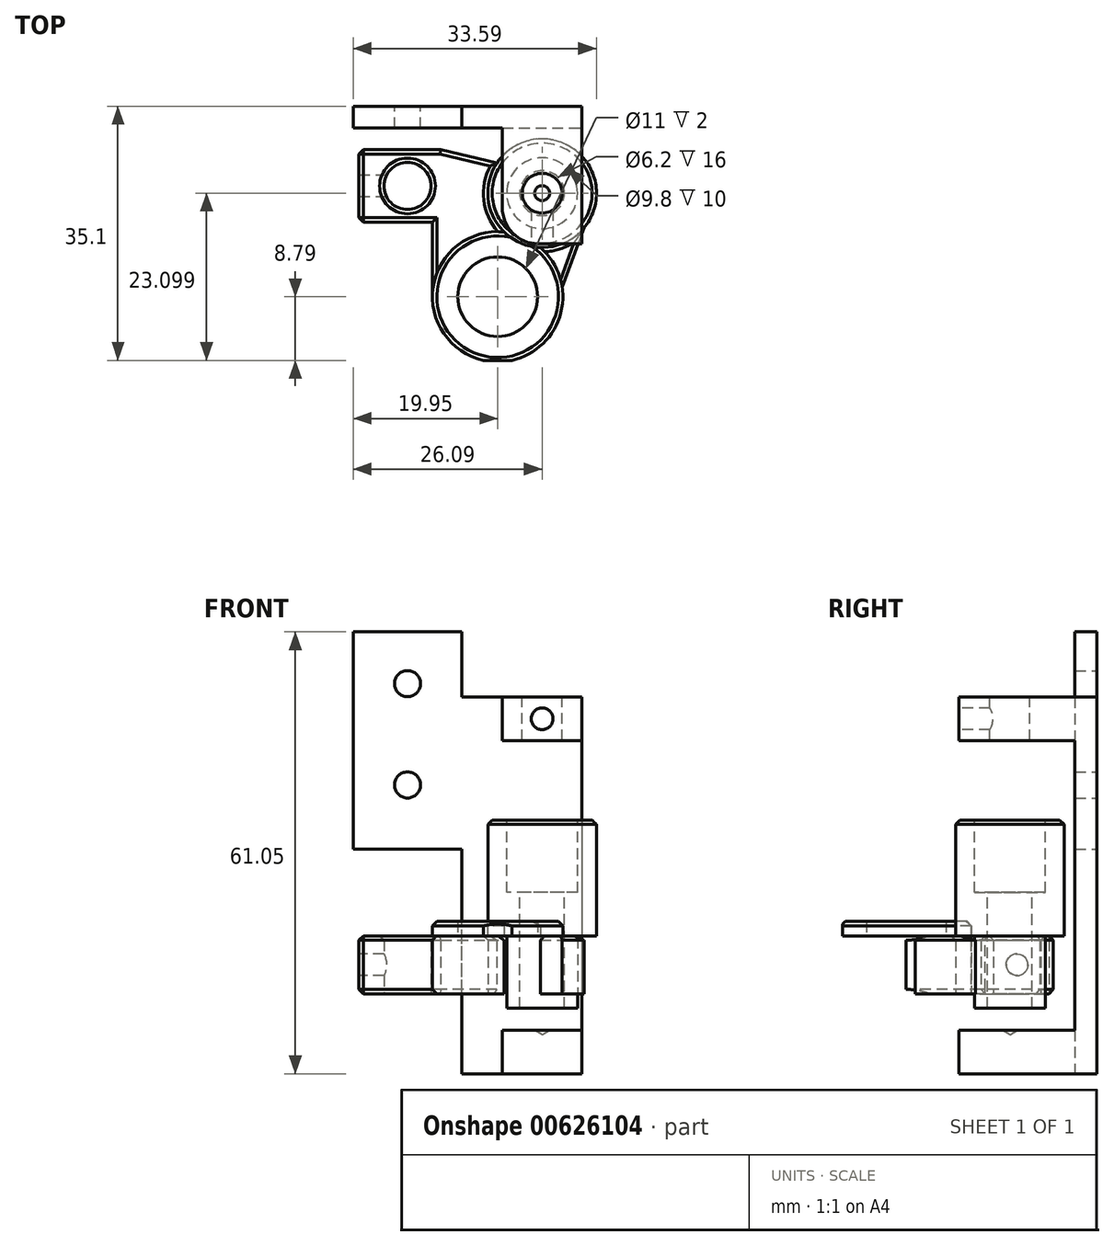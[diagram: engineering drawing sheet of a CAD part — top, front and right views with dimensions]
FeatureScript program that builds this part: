
annotation { "Feature Type Name" : "Feature", "Feature Type Description" : "" }
export const myFeature = defineFeature(function(context is Context, id is Id, definition is map)
    precondition{}
    {
        {
            var Q0;
            Q0=qCreatedBy(makeId("Top.planeOp"),FACE);
            var sketch = newSketch(context, id + "F0", { "sketchPlane" : qUnion([Q0])});
            skCircle(sketch, "E0", {"center": v(-12.45, 15.3) * mm, "radius": 3.25 * mm});
            skCircle(sketch, "E1", {"center": v(0, 0) * mm, "radius": 5.5 * mm});
            skCircle(sketch, "E2", {"center": v(6.14, 14.3) * mm, "radius": 4.9 * mm});
            skLineSegment(sketch, "E3", {"start": v(-26.15, 14.3) * mm, "end": v(35.58, 14.3) * mm, "construction": true});
            skLineSegment(sketch, "E4", {"start": v(-6.47, 0) * mm, "end": v(11.2, 0) * mm, "construction": true});
            skCircle(sketch, "E5", {"center": v(6.14, 14.3) * mm, "radius": 7.5 * mm});
            skLineSegment(sketch, "E6", {"start": v(0, 2.55) * mm, "end": v(0, -2.85) * mm, "construction": true});
            skLineSegment(sketch, "E7.bottom", {"start": v(-19.95, 22.8) * mm, "end": v(-4.95, 22.8) * mm, "construction": true});
            skLineSegment(sketch, "E7.top", {"start": v(-19.95, 7.8) * mm, "end": v(-4.95, 7.8) * mm, "construction": true});
            skLineSegment(sketch, "E7.right", {"start": v(-4.95, 22.8) * mm, "end": v(-4.95, 7.8) * mm, "construction": true});
            skLineSegment(sketch, "E8", {"start": v(-20.5, 15.3) * mm, "end": v(-2.43, 15.3) * mm, "construction": true});
            skLineSegment(sketch, "E9", {"start": v(-12.45, 21.65) * mm, "end": v(-12.45, 0) * mm, "construction": true});
            skLineSegment(sketch, "E10", {"start": v(-7.86, 20.3) * mm, "end": v(-19.16, 20.3) * mm});
            skLineSegment(sketch, "E11", {"start": v(-19.16, 20.3) * mm, "end": v(-19.16, 10.3) * mm});
            skLineSegment(sketch, "E12", {"start": v(-19.16, 10.3) * mm, "end": v(-9, 10.3) * mm});
            skCircle(sketch, "E13", {"center": v(6.14, 14.3) * mm, "radius": 3.1 * mm});
            skLineSegment(sketch, "E14", {"start": v(-19.95, 22.8) * mm, "end": v(-19.95, 7.8) * mm, "construction": true});
            skLineSegment(sketch, "E15", {"start": v(-9, 10.3) * mm, "end": v(-9, 0) * mm});
            skLineSegment(sketch, "E16", {"start": v(-7.86, 20.3) * mm, "end": v(-0.1, 18.47) * mm});
            skCircle(sketch, "E17", {"center": v(0, 0) * mm, "radius": 9 * mm});
            skLineSegment(sketch, "E18", {"start": v(8.9, 1.28) * mm, "end": v(11.93, 9.55) * mm});
            skLineSegment(sketch, "E19", {"start": v(-1.94, -8.79) * mm, "end": v(1.94, -8.79) * mm});
            skSolve(sketch);
        }
        {
            var Q0;
            Q0=makeQuery(id+"F0.imprint","IMPRINT",FACE,{"disambiguationData":[TD([[makeQuery(id+"F0.imprint","IMPRINT",EDGE,{"derivedFrom":sQuery(id+"F0.wireOp",EDGE,"E1")}),-1.0]])]});
            var Q1;
            {var subQ0=sQuery(id+"F0.wireOp",EDGE,"E17");var subQ1=sQuery(id+"F0.wireOp",EDGE,"E5");var subQ2=makeQuery(id+"F0.imprint","INTERSECT",VERTEX,{"disambiguationData":[OD(0.0)],"derivedFrom":[subQ1,subQ0]});Q1=makeQuery(id+"F0.imprint","IMPRINT",FACE,{"disambiguationData":[TD([[makeQuery(id+"F0.imprint","IMPRINT",EDGE,{"disambiguationData":[TD([[subQ2,-1.0]])],"derivedFrom":subQ1}),1.0]])]});}
            extrude(context, id + "F1", {"entities" : qUnion([Q0, Q1]), "endBound" : BoundingType.SYMMETRIC, "depth" : 12 * mm, "offsetDistance" : 25 * mm});
        }
        {
            var Q0;
            {var subQ0=sQuery(id+"F0.wireOp",EDGE,"E17");var subQ1=sQuery(id+"F0.wireOp",EDGE,"E5");var subQ2=makeQuery(id+"F0.imprint","INTERSECT",VERTEX,{"disambiguationData":[OD(0.0)],"derivedFrom":[subQ1,subQ0]});Q0=makeQuery(id+"F0.imprint","IMPRINT",FACE,{"disambiguationData":[TD([[makeQuery(id+"F0.imprint","IMPRINT",EDGE,{"disambiguationData":[TD([[subQ2,-1.0]])],"derivedFrom":subQ1}),1.0]])]});}
            var Q1;
            Q1=makeQuery(id+"F0.imprint","IMPRINT",FACE,{"disambiguationData":[TD([[makeQuery(id+"F0.imprint","IMPRINT",EDGE,{"derivedFrom":sQuery(id+"F0.wireOp",EDGE,"E2")}),-1.0]])]});
            var Q2;
            Q2=makeQuery(id+"F0.imprint","IMPRINT",FACE,{"disambiguationData":[TD([[makeQuery(id+"F0.imprint","IMPRINT",EDGE,{"derivedFrom":sQuery(id+"F0.wireOp",EDGE,"E2")}),1.0]])]});
            var Q3;
            Q3=makeQuery(id+"F1.opExtrude","CAP_FACE",FACE,{"disambiguationData":[OSD([sQuery(id+"F0.wireOp",EDGE,"E1"),sQuery(id+"F0.wireOp",EDGE,"E17")])],"isStart":true});
            extrude(context, id + "F2", {"entities" : qUnion([Q0, Q1, Q2]), "operationType" : NewBodyOperationType.ADD, "endBound" : BoundingType.UP_TO_SURFACE, "oppositeDirection" : true, "depth" : 20 * mm, "endBoundEntityFace" : qUnion([Q3]), "offsetDistance" : 25 * mm});
        }
        {
            var Q0;
            Q0=makeQuery(id+"F0.imprint","IMPRINT",FACE,{"disambiguationData":[TD([[makeQuery(id+"F0.imprint","IMPRINT",EDGE,{"derivedFrom":sQuery(id+"F0.wireOp",EDGE,"E0")}),-1.0]])]});
            var Q1;
            {var subQ0=sQuery(id+"F0.wireOp",EDGE,"E18");Q1=makeQuery(id+"F0.imprint","IMPRINT",FACE,{"disambiguationData":[TD([[makeQuery(id+"F0.imprint","IMPRINT",EDGE,{"derivedFrom":subQ0}),1.0]])]});}
            var Q2;
            Q2=makeQuery(id+"F1.opExtrude","CAP_FACE",FACE,{"disambiguationData":[OSD([sQuery(id+"F0.wireOp",EDGE,"E1"),sQuery(id+"F0.wireOp",EDGE,"E5"),sQuery(id+"F0.wireOp",EDGE,"E17")])],"isStart":false});
            extrude(context, id + "F3", {"entities" : qUnion([Q0, Q1]), "operationType" : NewBodyOperationType.ADD, "endBound" : BoundingType.SYMMETRIC, "depth" : 8 * mm, "endBoundEntityFace" : qUnion([Q2]), "offsetDistance" : 25 * mm});
        }
        {
            var Q0;
            {var subQ0=sQuery(id+"F0.wireOp",EDGE,"kT476SbK-n5dK-4PEZ-Ph8G-A7WMILJMmlgB");var subQ1=sQuery(id+"F0.wireOp",EDGE,"E5");var subQ2=makeQuery(id+"F0.imprint","INTERSECT",VERTEX,{"derivedFrom":[subQ1,subQ0]});Q0=makeQuery(id+"F0.imprint","IMPRINT",FACE,{"disambiguationData":[TD([[makeQuery(id+"F0.imprint","IMPRINT",EDGE,{"disambiguationData":[TD([[subQ2,-1.0]])],"derivedFrom":subQ1}),1.0]])]});}
            var Q1;
            Q1=makeQuery(id+"F0.imprint","IMPRINT",FACE,{"disambiguationData":[TD([[makeQuery(id+"F0.imprint","IMPRINT",EDGE,{"derivedFrom":sQuery(id+"F0.wireOp",EDGE,"E2")}),-1.0]])]});
            var Q2;
            Q2=makeQuery(id+"F0.imprint","IMPRINT",FACE,{"disambiguationData":[TD([[makeQuery(id+"F0.imprint","IMPRINT",EDGE,{"derivedFrom":sQuery(id+"F0.wireOp",EDGE,"E2")}),1.0]])]});
            var Q3;
            {var subQ0=sQuery(id+"F0.wireOp",EDGE,"E17");var subQ1=sQuery(id+"F0.wireOp",EDGE,"E5");var subQ2=makeQuery(id+"F0.imprint","INTERSECT",VERTEX,{"disambiguationData":[OD(0.0)],"derivedFrom":[subQ1,subQ0]});Q3=makeQuery(id+"F0.imprint","IMPRINT",FACE,{"disambiguationData":[TD([[makeQuery(id+"F0.imprint","IMPRINT",EDGE,{"disambiguationData":[TD([[subQ2,-1.0]])],"derivedFrom":subQ1}),1.0]])]});}
            var Q4;
            Q4=makeQuery(id+"F1.opExtrude","CAP_FACE",FACE,{"disambiguationData":[OSD([sQuery(id+"F0.wireOp",EDGE,"E1"),sQuery(id+"F0.wireOp",EDGE,"E17")])],"isStart":false});
            extrude(context, id + "F4", {"entities" : qUnion([Q0, Q1, Q2, Q3]), "operationType" : NewBodyOperationType.ADD, "depth" : 20 * mm, "endBoundEntityFace" : qUnion([Q4]), "offsetDistance" : 25 * mm});
        }
        {
            var Q0;
            Q0=makeQuery(id+"F4.opExtrude","CAP_FACE",FACE,{"disambiguationData":[OSD([sQuery(id+"F0.wireOp",EDGE,"E5"),sQuery(id+"F0.wireOp",EDGE,"E13")])],"isStart":false});
            var sketch = newSketch(context, id + "F5", { "sketchPlane" : qUnion([Q0])});
            skPoint(sketch, "E20.0", {"position": v(6.14, 14.3) * mm});
            skCircle(sketch, "E21.0", {"center": v(6.14, 14.3) * mm, "radius": 4.9 * mm});
            skCircle(sketch, "E22.0.0", {"center": v(6.14, 14.3) * mm, "radius": 7.5 * mm});
            skSolve(sketch);
        }
        {
            var Q0;
            Q0=makeQuery(id+"F5.imprint","IMPRINT",FACE,{"disambiguationData":[TD([[makeQuery(id+"F5.imprint","IMPRINT",EDGE,{"derivedFrom":sQuery(id+"F5.wireOp",EDGE,"E21.0")}),1.0]])]});
            extrude(context, id + "F6", {"entities" : qUnion([Q0]), "operationType" : NewBodyOperationType.REMOVE, "oppositeDirection" : true, "depth" : 10 * mm, "offsetDistance" : 25 * mm});
        }
        {
            var Q0;
            Q0=makeQuery(id+"F2.boolean.opBoolean","MERGE",FACE,{"derivedFrom":[makeQuery(id+"F1.opExtrude","CAP_FACE",FACE,{"disambiguationData":[OSD([sQuery(id+"F0.wireOp",EDGE,"E1"),sQuery(id+"F0.wireOp",EDGE,"E17"),sQuery(id+"F0.wireOp",EDGE,"E19")])],"isStart":true}),makeQuery(id+"F2.opExtrude","CAP_FACE",FACE,{"disambiguationData":[OSD([sQuery(id+"F0.wireOp",EDGE,"E5"),sQuery(id+"F0.wireOp",EDGE,"E13")])],"isStart":false})]});
            var sketch = newSketch(context, id + "F7", { "sketchPlane" : qUnion([Q0])});
            skCircle(sketch, "E23.0", {"center": v(6.14, -14.3) * mm, "radius": 4.9 * mm});
            skCircle(sketch, "E23.1", {"center": v(6.14, -14.3) * mm, "radius": 3.1 * mm});
            skCircle(sketch, "E24.0", {"center": v(6.14, -14.3) * mm, "radius": 3.9 * mm});
            skSolve(sketch);
        }
        {
            var Q0;
            Q0=makeQuery(id+"F7.imprint","IMPRINT",FACE,{"disambiguationData":[TD([[makeQuery(id+"F7.imprint","IMPRINT",EDGE,{"derivedFrom":sQuery(id+"F7.wireOp",EDGE,"E23.0")}),-1.0]])]});
            extrude(context, id + "F8", {"entities" : qUnion([Q0]), "operationType" : NewBodyOperationType.REMOVE, "oppositeDirection" : true, "depth" : 10 * mm, "offsetDistance" : 25 * mm});
        }
        {
            var Q0;
            Q0=makeQuery(id+"F3.opExtrude","SWEPT_FACE",FACE,{"disambiguationData":[OSD([sQuery(id+"F0.wireOp",EDGE,"E11")])]});
            var sketch = newSketch(context, id + "F9", { "sketchPlane" : qUnion([Q0])});
            skPoint(sketch, "E25.0", {"position": v(-15.3, 0) * mm});
            skSolve(sketch);
        }
        {
            var Q0;
            Q0=sQuery(id+"F9.wireOp",VERTEX,"E25.0");
            var Q1;
            Q1=makeQuery(id+"F1.opExtrude","SWEPT_BODY",BODY,{"disambiguationData":[OSD([sQuery(id+"F0.wireOp",EDGE,"E1"),sQuery(id+"F0.wireOp",EDGE,"E5"),sQuery(id+"F0.wireOp",EDGE,"kT476SbK-n5dK-4PEZ-Ph8G-A7WMILJMmlgB"),sQuery(id+"F0.wireOp",EDGE,"aIw4lDgL-LfnZ-en49-FZka-zHxeNgxKbi4w"),sQuery(id+"F0.wireOp",EDGE,"VI2pno59-77TE-V6qu-3BII-ZEAurTLzmaWP"),sQuery(id+"F0.wireOp",EDGE,"Tc2wsCnA-F8RX-Uh19-z4kL-r0QHivfHJg5U")])]});
            hole(context, id + "F10", {"style" : HoleStyle.SIMPLE, "endStyle" : HoleEndStyle.BLIND, "holeDiameter" : 3 * mm, "majorDiameter" : 5 * mm, "holeDepth" : 8 * mm, "isTappedThrough" : true, "tappedDepth" : 7 * mm, "tapClearance" : 6, "startFromSketch" : true, "locations" : qUnion([Q0]), "scope" : qUnion([Q1])});
        }
        {
            var Q0;
            Q0=makeQuery(id+"F1.opExtrude","SWEPT_FACE",FACE,{"disambiguationData":[OSD([sQuery(id+"F0.wireOp",EDGE,"E19")])]});
            var sketch = newSketch(context, id + "F11", { "sketchPlane" : qUnion([Q0])});
            skPoint(sketch, "E26.0", {"position": v(0, 0) * mm});
            skSolve(sketch);
        }
        {
            var Q0;
            Q0=sQuery(id+"F11.wireOp",VERTEX,"E26.0");
            var Q1;
            Q1=makeQuery(id+"F1.opExtrude","SWEPT_BODY",BODY,{"disambiguationData":[OSD([sQuery(id+"F0.wireOp",EDGE,"E1"),sQuery(id+"F0.wireOp",EDGE,"E5"),sQuery(id+"F0.wireOp",EDGE,"kT476SbK-n5dK-4PEZ-Ph8G-A7WMILJMmlgB"),sQuery(id+"F0.wireOp",EDGE,"aIw4lDgL-LfnZ-en49-FZka-zHxeNgxKbi4w"),sQuery(id+"F0.wireOp",EDGE,"VI2pno59-77TE-V6qu-3BII-ZEAurTLzmaWP"),sQuery(id+"F0.wireOp",EDGE,"Tc2wsCnA-F8RX-Uh19-z4kL-r0QHivfHJg5U")])]});
            hole(context, id + "F12", {"style" : HoleStyle.SIMPLE, "endStyle" : HoleEndStyle.BLIND, "holeDiameter" : 4.1 * mm, "majorDiameter" : 5 * mm, "holeDepth" : 8 * mm, "isTappedThrough" : true, "tappedDepth" : 7 * mm, "tapClearance" : 6, "startFromSketch" : true, "locations" : qUnion([Q0]), "scope" : qUnion([Q1])});
        }
        {
            var Q0;
            Q0=makeQuery(id+"F3.opExtrude","SWEPT_FACE",FACE,{"disambiguationData":[OSD([sQuery(id+"F0.wireOp",EDGE,"E10")])]});
            cPlane(context, id + "F13", {"entities" : qUnion([Q0]), "cplaneType" : CPlaneType.OFFSET, "offset" : 6 * mm, "width" : 150 * mm, "height" : 150 * mm});
        }
        {
            var Q0;
            Q0=qCreatedBy(id+"F13.planeOp",FACE);
            var sketch = newSketch(context, id + "F14", { "sketchPlane" : qUnion([Q0])});
            skLineSegment(sketch, "E27", {"start": v(19.95, 16) * mm, "end": v(19.95, 46) * mm});
            skLineSegment(sketch, "E28", {"start": v(-11.64, 36.98) * mm, "end": v(-11.64, -15.05) * mm});
            skLineSegment(sketch, "E29", {"start": v(-11.64, -15.05) * mm, "end": v(4.95, -15.05) * mm});
            skLineSegment(sketch, "E30", {"start": v(4.95, -15.05) * mm, "end": v(4.95, 16) * mm});
            skLineSegment(sketch, "E31", {"start": v(4.95, 16) * mm, "end": v(19.95, 16) * mm});
            skPoint(sketch, "E32.0", {"position": v(-6.14, 0) * mm});
            skLineSegment(sketch, "E33", {"start": v(-6.14, 34.02) * mm, "end": v(-6.14, -35.1) * mm, "construction": true});
            skLineSegment(sketch, "E34.bottom", {"start": v(-0.64, -9.05) * mm, "end": v(-11.64, -9.05) * mm});
            skLineSegment(sketch, "E34.top", {"start": v(-0.64, -15.05) * mm, "end": v(-11.64, -15.05) * mm});
            skLineSegment(sketch, "E34.left", {"start": v(-0.64, -9.05) * mm, "end": v(-0.64, -15.05) * mm});
            skLineSegment(sketch, "E34.right", {"start": v(-11.64, -9.05) * mm, "end": v(-11.64, -15.05) * mm});
            skLineSegment(sketch, "E35.bottom", {"start": v(-0.64, 36.98) * mm, "end": v(-11.64, 36.98) * mm});
            skLineSegment(sketch, "E35.top", {"start": v(-0.64, 30.98) * mm, "end": v(-11.64, 30.98) * mm});
            skLineSegment(sketch, "E35.left", {"start": v(-0.64, 36.98) * mm, "end": v(-0.64, 30.98) * mm});
            skLineSegment(sketch, "E35.right", {"start": v(-11.64, 36.98) * mm, "end": v(-11.64, 30.98) * mm});
            skPoint(sketch, "E36.0", {"position": v(12.45, 0) * mm});
            skLineSegment(sketch, "E37", {"start": v(12.45, 51.45) * mm, "end": v(12.45, -16.66) * mm, "construction": true});
            skLineSegment(sketch, "E38.0", {"start": v(19.16, 4) * mm, "end": v(19.16, 4) * mm});
            skLineSegment(sketch, "E39", {"start": v(-0.64, 36.98) * mm, "end": v(4.95, 36.98) * mm});
            skLineSegment(sketch, "E40", {"start": v(4.95, 36.98) * mm, "end": v(4.95, 46) * mm});
            skLineSegment(sketch, "E41", {"start": v(4.95, 46) * mm, "end": v(19.95, 46) * mm});
            skPoint(sketch, "E42", {"position": v(12.45, 38.84) * mm});
            skPoint(sketch, "E43", {"position": v(12.45, 24.84) * mm});
            skSolve(sketch);
        }
        {
            var Q0;
            Q0=makeQuery(id+"F14.imprint","IMPRINT",FACE,{"disambiguationData":[TD([[makeQuery(id+"F14.imprint","IMPRINT",EDGE,{"derivedFrom":sQuery(id+"F14.wireOp",EDGE,"E27")}),1.0]])]});
            extrude(context, id + "F15", {"entities" : qUnion([Q0]), "oppositeDirection" : true, "depth" : 3 * mm, "offsetDistance" : 25 * mm});
        }
        {
            var Q0;
            Q0=makeQuery(id+"F14.imprint","IMPRINT",FACE,{"disambiguationData":[TD([[makeQuery(id+"F14.imprint","IMPRINT",EDGE,{"derivedFrom":sQuery(id+"F14.wireOp",EDGE,"E35.bottom")}),1.0]])]});
            var Q1;
            Q1=makeQuery(id+"F14.imprint","IMPRINT",FACE,{"disambiguationData":[TD([[makeQuery(id+"F14.imprint","IMPRINT",EDGE,{"derivedFrom":sQuery(id+"F14.wireOp",EDGE,"E34.bottom")}),1.0]])]});
            extrude(context, id + "F16", {"entities" : qUnion([Q0, Q1]), "operationType" : NewBodyOperationType.ADD, "oppositeDirection" : true, "depth" : 19 * mm, "offsetDistance" : 25 * mm});
        }
        {
            var Q0;
            Q0=sQuery(id+"F14.wireOp",VERTEX,"E42");
            var Q1;
            Q1=sQuery(id+"F14.wireOp",VERTEX,"E43");
            var Q2;
            Q2=makeQuery(id+"F15.opExtrude","SWEPT_BODY",BODY,{"disambiguationData":[OSD([sQuery(id+"F14.wireOp",EDGE,"E27"),sQuery(id+"F14.wireOp",EDGE,"E28"),sQuery(id+"F14.wireOp",EDGE,"E29"),sQuery(id+"F14.wireOp",EDGE,"E30"),sQuery(id+"F14.wireOp",EDGE,"E31"),sQuery(id+"F14.wireOp",EDGE,"E34.bottom"),sQuery(id+"F14.wireOp",EDGE,"E34.left"),sQuery(id+"F14.wireOp",EDGE,"E35.top"),sQuery(id+"F14.wireOp",EDGE,"E35.left"),sQuery(id+"F14.wireOp",EDGE,"E39"),sQuery(id+"F14.wireOp",EDGE,"E40"),sQuery(id+"F14.wireOp",EDGE,"E41")])]});
            hole(context, id + "F17", {"style" : HoleStyle.SIMPLE, "endStyle" : HoleEndStyle.THROUGH, "holeDiameter" : 3.6 * mm, "majorDiameter" : 5 * mm, "isTappedThrough" : true, "tappedDepth" : 7 * mm, "tapClearance" : 6, "startFromSketch" : true, "locations" : qUnion([Q0, Q1]), "scope" : qUnion([Q2])});
        }
        {
            var Q0;
            {var subQ0=sQuery(id+"F14.wireOp",EDGE,"E35.bottom");var subQ1=sQuery(id+"F14.wireOp",EDGE,"t54O2XWj-5FLe-LaWo-9hj3-ZOWX0ZWZYv9O");Q0=makeQuery(id+"F16.boolean.opBoolean","MERGE",FACE,{"derivedFrom":[makeQuery(id+"F15.opExtrude","SWEPT_FACE",FACE,{"disambiguationData":[OSD([subQ1]),TDD([makeQuery(id+"F14.imprint","IMPRINT",EDGE,{"disambiguationData":[TD([[makeQuery(id+"F14.imprint","INTERSECT",VERTEX,{"derivedFrom":[sQuery(id+"F14.wireOp",EDGE,"E27"),subQ1]}),-1.0]])],"derivedFrom":subQ1})])]}),makeQuery(id+"F15.opExtrude","SWEPT_FACE",FACE,{"disambiguationData":[OSD([subQ1]),TDD([makeQuery(id+"F14.imprint","IMPRINT",EDGE,{"disambiguationData":[TD([[makeQuery(id+"F14.imprint","INTERSECT",VERTEX,{"derivedFrom":[subQ1,sQuery(id+"F14.wireOp",EDGE,"E28")]}),1.0]])],"derivedFrom":subQ1})])]}),makeQuery(id+"F16.opExtrude","SWEPT_FACE",FACE,{"disambiguationData":[OSD([subQ0])]})]});}
            var sketch = newSketch(context, id + "F18", { "sketchPlane" : qUnion([Q0])});
            skPoint(sketch, "E44.0", {"position": v(6.14, 14.3) * mm});
            skSolve(sketch);
        }
        {
            var Q0;
            Q0=sQuery(id+"F18.wireOp",VERTEX,"E44.0");
            var Q1;
            Q1=makeQuery(id+"F15.opExtrude","SWEPT_BODY",BODY,{"disambiguationData":[OSD([sQuery(id+"F14.wireOp",EDGE,"E27"),sQuery(id+"F14.wireOp",EDGE,"t54O2XWj-5FLe-LaWo-9hj3-ZOWX0ZWZYv9O"),sQuery(id+"F14.wireOp",EDGE,"E28"),sQuery(id+"F14.wireOp",EDGE,"E29"),sQuery(id+"F14.wireOp",EDGE,"E30"),sQuery(id+"F14.wireOp",EDGE,"E31"),sQuery(id+"F14.wireOp",EDGE,"E34.bottom"),sQuery(id+"F14.wireOp",EDGE,"E34.left"),sQuery(id+"F14.wireOp",EDGE,"E34.right"),sQuery(id+"F14.wireOp",EDGE,"E35.top"),sQuery(id+"F14.wireOp",EDGE,"E35.left"),sQuery(id+"F14.wireOp",EDGE,"E35.right")])]});
            hole(context, id + "F19", {"style" : HoleStyle.SIMPLE, "endStyle" : HoleEndStyle.BLIND, "holeDiameter" : 5.5 * mm, "majorDiameter" : 5 * mm, "holeDepth" : 45 * mm, "isTappedThrough" : true, "tappedDepth" : 7 * mm, "tapClearance" : 6, "startFromSketch" : true, "locations" : qUnion([Q0]), "scope" : qUnion([Q1])});
        }
        {
            var Q0;
            Q0=makeQuery(id+"F16.opExtrude","CAP_EDGE",EDGE,{"disambiguationData":[OSD([sQuery(id+"F14.wireOp",EDGE,"E35.left")])],"isStart":false});
            var Q1;
            Q1=makeQuery(id+"F16.opExtrude","CAP_EDGE",EDGE,{"disambiguationData":[OSD([sQuery(id+"F14.wireOp",EDGE,"E35.right")])],"isStart":false});
            var Q2;
            Q2=makeQuery(id+"F16.opExtrude","CAP_EDGE",EDGE,{"disambiguationData":[OSD([sQuery(id+"F14.wireOp",EDGE,"E34.left")])],"isStart":false});
            var Q3;
            Q3=makeQuery(id+"F16.opExtrude","CAP_EDGE",EDGE,{"disambiguationData":[OSD([sQuery(id+"F14.wireOp",EDGE,"E34.right")])],"isStart":false});
            fillet(context, id + "F20", {"entities" : qUnion([Q0, Q1, Q2, Q3]), "radius" : 5 * mm, "tangentPropagation" : true, "allowEdgeOverflow" : false});
        }
        {
            var Q0;
            Q0=makeQuery(id+"F16.opExtrude","CAP_FACE",FACE,{"disambiguationData":[OSD([sQuery(id+"F14.wireOp",EDGE,"E35.bottom"),sQuery(id+"F14.wireOp",EDGE,"E35.top"),sQuery(id+"F14.wireOp",EDGE,"E35.left"),sQuery(id+"F14.wireOp",EDGE,"E35.right")])],"isStart":false});
            var sketch = newSketch(context, id + "F21", { "sketchPlane" : qUnion([Q0])});
            skLineSegment(sketch, "E45.1", {"start": v(0.64, 36.98) * mm, "end": v(11.64, 36.98) * mm});
            skLineSegment(sketch, "E45.2", {"start": v(5.64, 36.98) * mm, "end": v(6.64, 36.98) * mm});
            skLineSegment(sketch, "E45.3", {"start": v(5.64, 30.98) * mm, "end": v(6.64, 30.98) * mm});
            skPoint(sketch, "E46", {"position": v(6.14, 36.98) * mm});
            skPoint(sketch, "E47.0", {"position": v(5.64, 33.98) * mm});
            skPoint(sketch, "E48", {"position": v(6.14, 33.98) * mm});
            skPoint(sketch, "E49.0", {"position": v(5.64, -12.05) * mm});
            skPoint(sketch, "E50.0", {"position": v(6.14, -9.05) * mm});
            skPoint(sketch, "E51", {"position": v(6.14, -12.05) * mm});
            skSolve(sketch);
        }
        {
            var Q0;
            Q0=sQuery(id+"F21.wireOp",VERTEX,"E48");
            var Q1;
            Q1=makeQuery(id+"F15.opExtrude","SWEPT_BODY",BODY,{"disambiguationData":[OSD([sQuery(id+"F14.wireOp",EDGE,"E27"),sQuery(id+"F14.wireOp",EDGE,"E28"),sQuery(id+"F14.wireOp",EDGE,"E29"),sQuery(id+"F14.wireOp",EDGE,"E30"),sQuery(id+"F14.wireOp",EDGE,"E31"),sQuery(id+"F14.wireOp",EDGE,"E34.bottom"),sQuery(id+"F14.wireOp",EDGE,"E34.left"),sQuery(id+"F14.wireOp",EDGE,"E35.top"),sQuery(id+"F14.wireOp",EDGE,"E35.left"),sQuery(id+"F14.wireOp",EDGE,"E39"),sQuery(id+"F14.wireOp",EDGE,"E40"),sQuery(id+"F14.wireOp",EDGE,"E41")])]});
            hole(context, id + "F22", {"style" : HoleStyle.SIMPLE, "endStyle" : HoleEndStyle.BLIND, "holeDiameter" : 3 * mm, "majorDiameter" : 5 * mm, "holeDepth" : 5 * mm, "isTappedThrough" : true, "tappedDepth" : 7 * mm, "tapClearance" : 6, "startFromSketch" : true, "locations" : qUnion([Q0]), "scope" : qUnion([Q1])});
        }
        {
            var Q0;
            Q0=makeQuery(id+"F6.boolean.opBoolean","COPY",EDGE,{"derivedFrom":makeQuery(id+"F6.opExtrude","CAP_EDGE",EDGE,{"disambiguationData":[OSD([sQuery(id+"F5.wireOp",EDGE,"E21.0")])],"isStart":true})});
            var Q1;
            Q1=makeQuery(id+"F3.opExtrude","CAP_EDGE",EDGE,{"disambiguationData":[OSD([sQuery(id+"F0.wireOp",EDGE,"E0")])],"isStart":false});
            var Q2;
            Q2=makeQuery(id+"F8.boolean.opBoolean","COPY",EDGE,{"derivedFrom":makeQuery(id+"F8.opExtrude","CAP_EDGE",EDGE,{"disambiguationData":[OSD([sQuery(id+"F7.wireOp",EDGE,"E23.0")])],"isStart":true})});
            chamfer(context, id + "F23", {"entities" : qUnion([Q0, Q1, Q2]), "width" : 0.6 * mm, "tangentPropagation" : true});
        }
        {
            var Q0;
            Q0=makeQuery(id+"F4.boolean.opBoolean","SPLIT",EDGE,{"disambiguationData":[OD(0.0)],"derivedFrom":makeQuery(id+"F1.opExtrude","CAP_EDGE",EDGE,{"disambiguationData":[OSD([sQuery(id+"F0.wireOp",EDGE,"E17")])],"isStart":false})});
            var Q1;
            Q1=makeQuery(id+"F4.boolean.opBoolean","SPLIT",EDGE,{"disambiguationData":[OD(1.0)],"derivedFrom":makeQuery(id+"F1.opExtrude","CAP_EDGE",EDGE,{"disambiguationData":[OSD([sQuery(id+"F0.wireOp",EDGE,"E17")])],"isStart":false})});
            var Q2;
            Q2=makeQuery(id+"F3.opExtrude","CAP_EDGE",EDGE,{"disambiguationData":[OSD([sQuery(id+"F0.wireOp",EDGE,"E15")])],"isStart":false});
            var Q3;
            Q3=makeQuery(id+"F3.opExtrude","CAP_EDGE",EDGE,{"disambiguationData":[OSD([sQuery(id+"F0.wireOp",EDGE,"E12")])],"isStart":false});
            var Q4;
            Q4=makeQuery(id+"F3.opExtrude","CAP_EDGE",EDGE,{"disambiguationData":[OSD([sQuery(id+"F0.wireOp",EDGE,"E11")])],"isStart":false});
            var Q5;
            Q5=makeQuery(id+"F3.opExtrude","CAP_EDGE",EDGE,{"disambiguationData":[OSD([sQuery(id+"F0.wireOp",EDGE,"E10")])],"isStart":false});
            var Q6;
            Q6=makeQuery(id+"F3.opExtrude","CAP_EDGE",EDGE,{"disambiguationData":[OSD([sQuery(id+"F0.wireOp",EDGE,"E16")])],"isStart":false});
            var Q7;
            {var subQ0=sQuery(id+"F0.wireOp",EDGE,"E5");Q7=makeQuery(id+"F3.opExtrude","CAP_EDGE",EDGE,{"disambiguationData":[OSD([subQ0]),TDD([makeQuery(id+"F0.imprint","IMPRINT",EDGE,{"disambiguationData":[TD([[makeQuery(id+"F0.imprint","INTERSECT",VERTEX,{"derivedFrom":[subQ0,sQuery(id+"F0.wireOp",EDGE,"E16")]}),-1.0]])],"derivedFrom":subQ0})])],"isStart":false});}
            var Q8;
            Q8=makeQuery(id+"F3.opExtrude","CAP_EDGE",EDGE,{"disambiguationData":[OSD([sQuery(id+"F0.wireOp",EDGE,"E18")])],"isStart":false});
            var Q9;
            {var subQ0=sQuery(id+"F0.wireOp",EDGE,"E5");Q9=makeQuery(id+"F3.opExtrude","CAP_EDGE",EDGE,{"disambiguationData":[OSD([subQ0]),TDD([makeQuery(id+"F0.imprint","IMPRINT",EDGE,{"disambiguationData":[TD([[makeQuery(id+"F0.imprint","INTERSECT",VERTEX,{"derivedFrom":[subQ0,sQuery(id+"F0.wireOp",EDGE,"E18")]}),1.0]])],"derivedFrom":subQ0})])],"isStart":false});}
            var Q10;
            {var subQ0=sQuery(id+"F0.wireOp",EDGE,"E17");Q10=makeQuery(id+"F3.opExtrude","CAP_EDGE",EDGE,{"disambiguationData":[OSD([subQ0]),TDD([makeQuery(id+"F0.imprint","IMPRINT",EDGE,{"disambiguationData":[TD([[makeQuery(id+"F0.imprint","INTERSECT",VERTEX,{"derivedFrom":[subQ0,sQuery(id+"F0.wireOp",EDGE,"E18")]}),-1.0]])],"derivedFrom":subQ0})])],"isStart":false});}
            var Q11;
            Q11=makeQuery(id+"F4.opExtrude","CAP_EDGE",EDGE,{"disambiguationData":[OSD([sQuery(id+"F0.wireOp",EDGE,"E5")])],"isStart":false});
            var Q12;
            Q12=makeQuery(id+"F2.opExtrude","CAP_EDGE",EDGE,{"disambiguationData":[OSD([sQuery(id+"F0.wireOp",EDGE,"E5")])],"isStart":false});
            var Q13;
            Q13=makeQuery(id+"F3.opExtrude","CAP_EDGE",EDGE,{"disambiguationData":[OSD([sQuery(id+"F0.wireOp",EDGE,"E12")])],"isStart":true});
            var Q14;
            Q14=makeQuery(id+"F3.opExtrude","CAP_EDGE",EDGE,{"disambiguationData":[OSD([sQuery(id+"F0.wireOp",EDGE,"E15")])],"isStart":true});
            var Q15;
            Q15=makeQuery(id+"F3.opExtrude","CAP_EDGE",EDGE,{"disambiguationData":[OSD([sQuery(id+"F0.wireOp",EDGE,"E10")])],"isStart":true});
            var Q16;
            Q16=makeQuery(id+"F3.opExtrude","CAP_EDGE",EDGE,{"disambiguationData":[OSD([sQuery(id+"F0.wireOp",EDGE,"E11")])],"isStart":true});
            var Q17;
            Q17=makeQuery(id+"F3.opExtrude","CAP_EDGE",EDGE,{"disambiguationData":[OSD([sQuery(id+"F0.wireOp",EDGE,"E16")])],"isStart":true});
            var Q18;
            Q18=makeQuery(id+"F3.opExtrude","SWEPT_EDGE",EDGE,{"disambiguationData":[OSD([sQuery(id+"F0.wireOp",EDGE,"E11"),sQuery(id+"F0.wireOp",EDGE,"E12")])]});
            var Q19;
            Q19=makeQuery(id+"F3.opExtrude","SWEPT_EDGE",EDGE,{"disambiguationData":[OSD([sQuery(id+"F0.wireOp",EDGE,"E10"),sQuery(id+"F0.wireOp",EDGE,"E11")])]});
            chamfer(context, id + "F24", {"entities" : qUnion([Q0, Q1, Q2, Q3, Q4, Q5, Q6, Q7, Q8, Q9, Q10, Q11, Q12, Q13, Q14, Q15, Q16, Q17, Q18, Q19]), "width" : 0.6 * mm, "tangentPropagation" : true});
        }
    });
